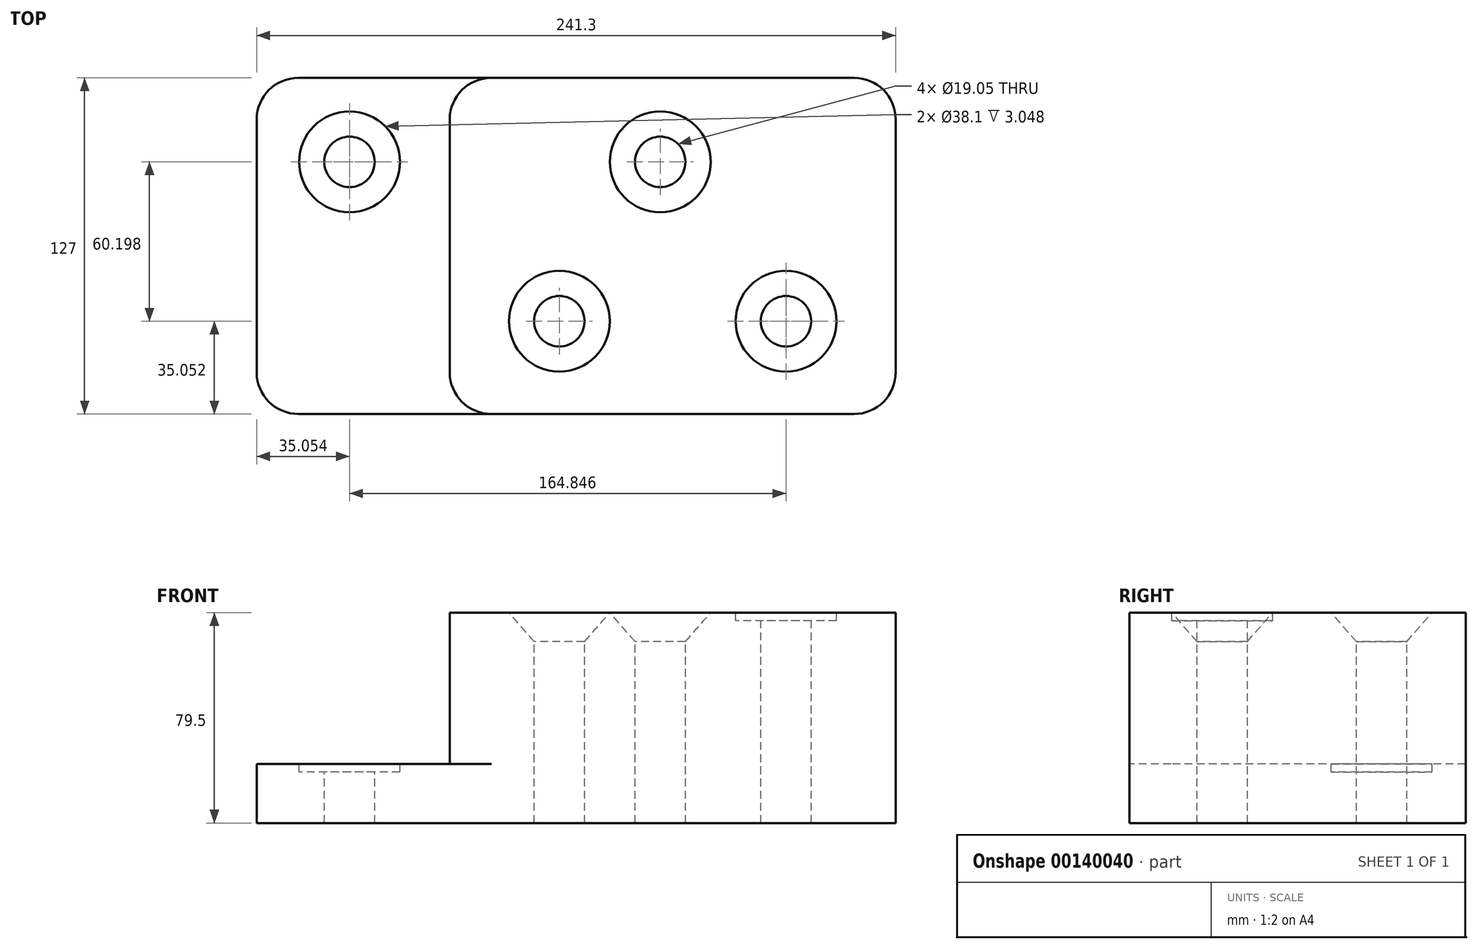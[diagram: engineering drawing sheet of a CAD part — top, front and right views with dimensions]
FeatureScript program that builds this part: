
annotation { "Feature Type Name" : "Feature", "Feature Type Description" : "" }
export const myFeature = defineFeature(function(context is Context, id is Id, definition is map)
    precondition{}
    {
        {
            var Q0;
            Q0=qCreatedBy(makeId("Top.planeOp"),FACE);
            var sketch = newSketch(context, id + "F0", { "sketchPlane" : qUnion([Q0])});
            skLineSegment(sketch, "E0.bottom", {"start": v(15.75, 127) * mm, "end": v(152.65, 127) * mm});
            skLineSegment(sketch, "E0.top", {"start": v(15.75, 0) * mm, "end": v(152.65, 0) * mm});
            skLineSegment(sketch, "E0.left", {"start": v(0, 111.25) * mm, "end": v(0, 15.75) * mm});
            skLineSegment(sketch, "E0.right", {"start": v(168.4, 111.25) * mm, "end": v(168.4, 15.75) * mm});
            skArc(sketch, "E1.filletArc", {"start": v(15.75, 127) * mm, "mid": v(4.61, 122.39) * mm, "end": v(0, 111.25) * mm});
            skPoint(sketch, "E2.visualSharp", {"position": v(168.4, 127) * mm});
            skArc(sketch, "E2.filletArc", {"start": v(168.4, 111.25) * mm, "mid": v(163.79, 122.39) * mm, "end": v(152.65, 127) * mm});
            skPoint(sketch, "E3.visualSharp", {"position": v(168.4, 0) * mm});
            skArc(sketch, "E3.filletArc", {"start": v(152.65, 0) * mm, "mid": v(163.79, 4.61) * mm, "end": v(168.4, 15.75) * mm});
            skPoint(sketch, "E4.visualSharp", {"position": v(0, 0) * mm});
            skArc(sketch, "E4.filletArc", {"start": v(0, 15.75) * mm, "mid": v(4.61, 4.61) * mm, "end": v(15.75, 0) * mm});
            skLineSegment(sketch, "E5", {"start": v(15.75, 0) * mm, "end": v(-57.15, 0) * mm});
            skLineSegment(sketch, "E6", {"start": v(-72.9, 15.75) * mm, "end": v(-72.9, 111.25) * mm});
            skLineSegment(sketch, "E7", {"start": v(-57.15, 127) * mm, "end": v(15.75, 127) * mm});
            skPoint(sketch, "E8.visualSharp", {"position": v(-72.9, 127) * mm});
            skArc(sketch, "E8.filletArc", {"start": v(-57.15, 127) * mm, "mid": v(-68.29, 122.39) * mm, "end": v(-72.9, 111.25) * mm});
            skPoint(sketch, "E9.visualSharp", {"position": v(-72.9, 0) * mm});
            skArc(sketch, "E9.filletArc", {"start": v(-72.9, 15.75) * mm, "mid": v(-68.29, 4.61) * mm, "end": v(-57.15, 0) * mm});
            skPoint(sketch, "E10", {"position": v(-37.85, 95.25) * mm});
            skPoint(sketch, "E11", {"position": v(79.5, 95.25) * mm});
            skPoint(sketch, "E12", {"position": v(127, 35.05) * mm});
            skPoint(sketch, "E13", {"position": v(41.4, 35.05) * mm});
            skSolve(sketch);
        }
        {
            var Q0;
            Q0=makeQuery(id+"F0.imprint","IMPRINT",FACE,{"disambiguationData":[TD([[makeQuery(id+"F0.imprint","IMPRINT",EDGE,{"derivedFrom":sQuery(id+"F0.wireOp",EDGE,"E0.bottom")}),-1.0]])]});
            extrude(context, id + "F1", {"entities" : qUnion([Q0]), "depth" : 79.5 * mm});
        }
        {
            var Q0;
            Q0=makeQuery(id+"F0.imprint","IMPRINT",FACE,{"disambiguationData":[TD([[makeQuery(id+"F0.imprint","IMPRINT",EDGE,{"derivedFrom":sQuery(id+"F0.wireOp",EDGE,"E0.left")}),-1.0]])]});
            extrude(context, id + "F2", {"entities" : qUnion([Q0]), "operationType" : NewBodyOperationType.ADD, "depth" : 22.35 * mm});
        }
        {
            var Q0;
            Q0=makeQuery(id+"F1.opExtrude","CAP_FACE",FACE,{"disambiguationData":[OSD([sQuery(id+"F0.wireOp",EDGE,"E0.bottom"),sQuery(id+"F0.wireOp",EDGE,"E0.top"),sQuery(id+"F0.wireOp",EDGE,"E0.left"),sQuery(id+"F0.wireOp",EDGE,"E0.right"),sQuery(id+"F0.wireOp",EDGE,"E1.filletArc"),sQuery(id+"F0.wireOp",EDGE,"E2.filletArc"),sQuery(id+"F0.wireOp",EDGE,"E3.filletArc"),sQuery(id+"F0.wireOp",EDGE,"E4.filletArc")])],"isStart":false});
            var sketch = newSketch(context, id + "F3", { "sketchPlane" : qUnion([Q0])});
            skPoint(sketch, "E14.0", {"position": v(79.5, 95.25) * mm});
            skPoint(sketch, "E15.0", {"position": v(127, 35.05) * mm});
            skPoint(sketch, "E16.0", {"position": v(41.4, 35.05) * mm});
            skPoint(sketch, "E17.0", {"position": v(-37.85, 95.25) * mm});
            skSolve(sketch);
        }
        {
            var Q0;
            Q0=sQuery(id+"F3.wireOp",VERTEX,"E16.0");
            var Q1;
            Q1=makeQuery(id+"F1.opExtrude","SWEPT_BODY",BODY,{"disambiguationData":[OSD([sQuery(id+"F0.wireOp",EDGE,"E0.bottom"),sQuery(id+"F0.wireOp",EDGE,"E0.top"),sQuery(id+"F0.wireOp",EDGE,"E0.left"),sQuery(id+"F0.wireOp",EDGE,"E0.right"),sQuery(id+"F0.wireOp",EDGE,"E1.filletArc"),sQuery(id+"F0.wireOp",EDGE,"E2.filletArc"),sQuery(id+"F0.wireOp",EDGE,"E3.filletArc"),sQuery(id+"F0.wireOp",EDGE,"E4.filletArc")])]});
            hole(context, id + "F4", {"style" : HoleStyle.C_SINK, "endStyle" : HoleEndStyle.THROUGH, "holeDiameter" : 19.05 * mm, "cSinkDiameter" : 38.1 * mm, "cSinkAngle" : 82 * degree, "locations" : qUnion([Q0]), "scope" : qUnion([Q1]), "isTappedThrough" : true});
        }
        {
            var Q0;
            Q0=sQuery(id+"F3.wireOp",VERTEX,"E14.0");
            var Q1;
            Q1=makeQuery(id+"F1.opExtrude","SWEPT_BODY",BODY,{"disambiguationData":[OSD([sQuery(id+"F0.wireOp",EDGE,"E0.bottom"),sQuery(id+"F0.wireOp",EDGE,"E0.top"),sQuery(id+"F0.wireOp",EDGE,"E0.left"),sQuery(id+"F0.wireOp",EDGE,"E0.right"),sQuery(id+"F0.wireOp",EDGE,"E1.filletArc"),sQuery(id+"F0.wireOp",EDGE,"E2.filletArc"),sQuery(id+"F0.wireOp",EDGE,"E3.filletArc"),sQuery(id+"F0.wireOp",EDGE,"E4.filletArc")])]});
            hole(context, id + "F5", {"style" : HoleStyle.C_SINK, "endStyle" : HoleEndStyle.THROUGH, "holeDiameter" : 19.05 * mm, "cSinkDiameter" : 38.1 * mm, "cSinkAngle" : 82 * degree, "locations" : qUnion([Q0]), "scope" : qUnion([Q1]), "isTappedThrough" : true});
        }
        {
            var Q0;
            Q0=sQuery(id+"F3.wireOp",VERTEX,"E15.0");
            var Q1;
            Q1=makeQuery(id+"F1.opExtrude","SWEPT_BODY",BODY,{"disambiguationData":[OSD([sQuery(id+"F0.wireOp",EDGE,"E0.bottom"),sQuery(id+"F0.wireOp",EDGE,"E0.top"),sQuery(id+"F0.wireOp",EDGE,"E0.left"),sQuery(id+"F0.wireOp",EDGE,"E0.right"),sQuery(id+"F0.wireOp",EDGE,"E1.filletArc"),sQuery(id+"F0.wireOp",EDGE,"E2.filletArc"),sQuery(id+"F0.wireOp",EDGE,"E3.filletArc"),sQuery(id+"F0.wireOp",EDGE,"E4.filletArc")])]});
            hole(context, id + "F6", {"style" : HoleStyle.C_BORE, "endStyle" : HoleEndStyle.THROUGH, "holeDiameter" : 19.05 * mm, "cBoreDiameter" : 38.1 * mm, "cBoreDepth" : 3.05 * mm, "locations" : qUnion([Q0]), "scope" : qUnion([Q1]), "isTappedThrough" : true});
        }
        {
            var Q0;
            Q0=makeQuery(id+"F2.opExtrude","CAP_FACE",FACE,{"disambiguationData":[OSD([sQuery(id+"F0.wireOp",EDGE,"E0.left"),sQuery(id+"F0.wireOp",EDGE,"E1.filletArc"),sQuery(id+"F0.wireOp",EDGE,"E4.filletArc"),sQuery(id+"F0.wireOp",EDGE,"E5"),sQuery(id+"F0.wireOp",EDGE,"E6"),sQuery(id+"F0.wireOp",EDGE,"E7"),sQuery(id+"F0.wireOp",EDGE,"E8.filletArc"),sQuery(id+"F0.wireOp",EDGE,"E9.filletArc")])],"isStart":false});
            var sketch = newSketch(context, id + "F7", { "sketchPlane" : qUnion([Q0])});
            skPoint(sketch, "E18.0", {"position": v(-37.85, 95.25) * mm});
            skSolve(sketch);
        }
        {
            var Q0;
            Q0=sQuery(id+"F7.wireOp",VERTEX,"E18.0");
            var Q1;
            Q1=makeQuery(id+"F1.opExtrude","SWEPT_BODY",BODY,{"disambiguationData":[OSD([sQuery(id+"F0.wireOp",EDGE,"E0.bottom"),sQuery(id+"F0.wireOp",EDGE,"E0.top"),sQuery(id+"F0.wireOp",EDGE,"E0.left"),sQuery(id+"F0.wireOp",EDGE,"E0.right"),sQuery(id+"F0.wireOp",EDGE,"E1.filletArc"),sQuery(id+"F0.wireOp",EDGE,"E2.filletArc"),sQuery(id+"F0.wireOp",EDGE,"E3.filletArc"),sQuery(id+"F0.wireOp",EDGE,"E4.filletArc")])]});
            hole(context, id + "F8", {"style" : HoleStyle.C_BORE, "endStyle" : HoleEndStyle.THROUGH, "holeDiameter" : 19.05 * mm, "cBoreDiameter" : 38.1 * mm, "cBoreDepth" : 3.05 * mm, "locations" : qUnion([Q0]), "scope" : qUnion([Q1]), "isTappedThrough" : true});
        }
    });
